# Revit family: Wall-Panel_Metal-Rainscreen
name_source: partatom
category: Curtain Panels
units: mm (PartAtom-declared; Revit-internal decimal feet)

## family parameters
Always vertical = Yes
Classification Number = 23.35.06.21.10
Cut with Voids When Loaded = No
Shared = No

## types (1)
- ByType
    Assembly Code = B20
    Channel Depth = 0' - 1"
    Cladding Material-Finish = ARCAT - Metal - Aluminum_0.032" - Burgundy
    Cladding Thickness = 0' - 0 1/16"
    Clip Offset = 0' - 1"
    Clips-Panel = 3
    Construction Details = http://www.arcat.com
    Description = Metal Rainscreen Panel
    Expected Lifespan (Years) = 30
    Green Building-LEED = http://www.arcat.com
    Hardware Material = ARCAT - Metal - Aluminum_0.032" - Mill
    Keynote = 07410
    Maintenance Schedule (Months) = 24
    Manufacturer = "Generic"
    Manufacturer Fax = (203) 929-2444
    Manufacturer Website = http://www.arcat.com
    Model = "Generic"
    Offset = 0' - 0 3/8"
    Panel Thickness = 0' - 1"
    Product Data = http://www.arcat.com
    Product Properties = http://www.arcat.com
    Specification = http://www.arcat.com
    Tongue Length = 0' - 2 1/8"
    Warranty Duration (Years) = 10
